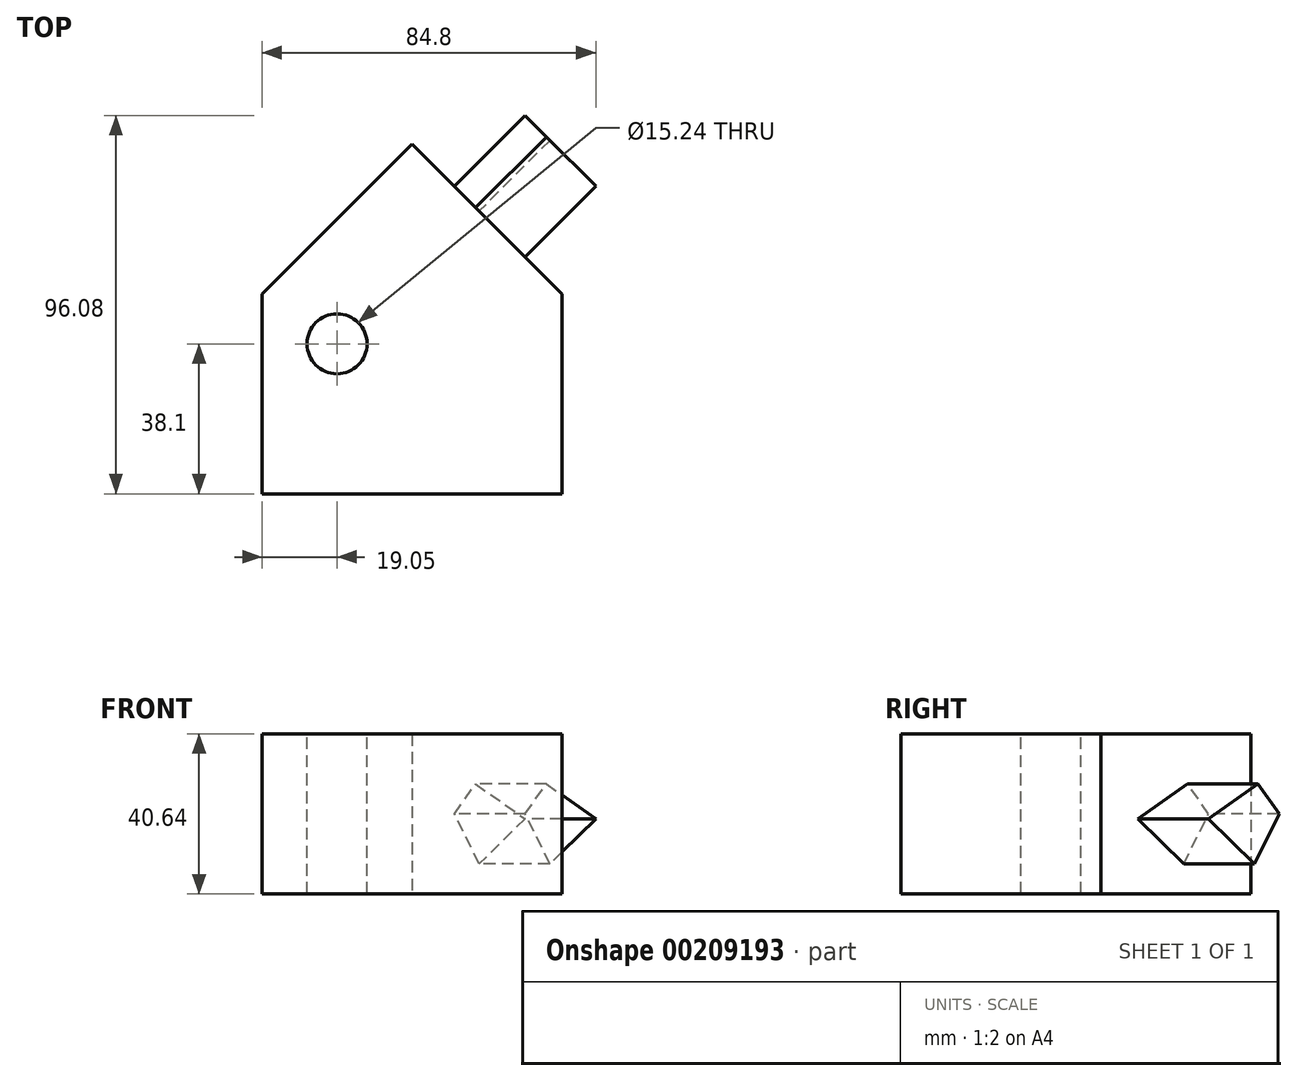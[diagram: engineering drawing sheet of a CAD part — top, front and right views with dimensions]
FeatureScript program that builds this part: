
annotation { "Feature Type Name" : "Feature", "Feature Type Description" : "" }
export const myFeature = defineFeature(function(context is Context, id is Id, definition is map)
    precondition{}
    {
        {
            var Q0;
            Q0=qCreatedBy(makeId("Top.planeOp"),FACE);
            var sketch = newSketch(context, id + "F0", { "sketchPlane" : qUnion([Q0])});
            skLineSegment(sketch, "E0.bottom", {"start": v(0, 0) * mm, "end": v(76.2, 0) * mm});
            skLineSegment(sketch, "E0.top", {"start": v(0, 50.8) * mm, "end": v(76.2, 50.8) * mm});
            skLineSegment(sketch, "E0.left", {"start": v(0, 0) * mm, "end": v(0, 50.8) * mm});
            skLineSegment(sketch, "E0.right", {"start": v(76.2, 0) * mm, "end": v(76.2, 50.8) * mm});
            skLineSegment(sketch, "E1", {"start": v(0, 50.8) * mm, "end": v(38.1, 88.9) * mm});
            skLineSegment(sketch, "E2", {"start": v(38.1, 88.9) * mm, "end": v(76.2, 50.8) * mm});
            skSolve(sketch);
        }
        {
            var Q0;
            Q0 = qSketchRegion(id + "F0", true);
            extrude(context, id + "F1", {"entities" : qUnion([Q0]), "depth" : 40.64 * mm});
        }
        {
            var Q0;
            Q0=makeQuery(id+"F1.opExtrude","CAP_FACE",FACE,{"disambiguationData":[OSD([sQuery(id+"F0.wireOp",EDGE,"E0.bottom"),sQuery(id+"F0.wireOp",EDGE,"E0.left"),sQuery(id+"F0.wireOp",EDGE,"E0.right"),sQuery(id+"F0.wireOp",EDGE,"E1"),sQuery(id+"F0.wireOp",EDGE,"E2")])],"isStart":false});
            var sketch = newSketch(context, id + "F2", { "sketchPlane" : qUnion([Q0])});
            skCircle(sketch, "E3", {"center": v(19.05, 38.1) * mm, "radius": 7.62 * mm});
            skSolve(sketch);
        }
        {
            var Q0;
            Q0 = qSketchRegion(id + "F2", true);
            extrude(context, id + "F3", {"entities" : qUnion([Q0]), "operationType" : NewBodyOperationType.REMOVE, "endBound" : BoundingType.THROUGH_ALL, "oppositeDirection" : true, "depth" : 25.4 * mm});
        }
        {
            var Q0;
            Q0=makeQuery(id+"F1.opExtrude","SWEPT_FACE",FACE,{"disambiguationData":[OSD([sQuery(id+"F0.wireOp",EDGE,"E2")])]});
            var sketch = newSketch(context, id + "F4", { "sketchPlane" : qUnion([Q0])});
            skLineSegment(sketch, "E4", {"start": v(20.68, 20.32) * mm, "end": v(13.06, 27.94) * mm});
            skLineSegment(sketch, "E5", {"start": v(13.06, 27.94) * mm, "end": v(-4.72, 19.05) * mm});
            skLineSegment(sketch, "E6", {"start": v(-4.72, 19.05) * mm, "end": v(11.8, 7.62) * mm});
            skLineSegment(sketch, "E7", {"start": v(11.8, 7.62) * mm, "end": v(20.68, 20.32) * mm});
            skSolve(sketch);
        }
        {
            var Q0;
            Q0 = qSketchRegion(id + "F4", true);
            extrude(context, id + "F5", {"entities" : qUnion([Q0]), "depth" : 25.4 * mm});
        }
    });
